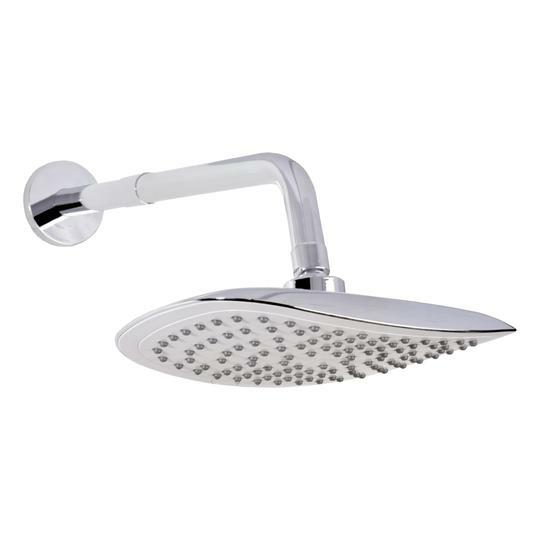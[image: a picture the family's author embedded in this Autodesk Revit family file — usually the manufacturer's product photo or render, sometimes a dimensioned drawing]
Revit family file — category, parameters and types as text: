
# Revit family: 01-1435-11 MEZCLADOR DUCHA 8” SIN SALIDA TOSCANA
name_source: partatom
category: Plumbing Fixtures
revit_build: Autodesk Revit 2018 (Build: 20170223_1515(x64)
units: mm (PartAtom-declared; Revit-internal decimal feet)

## family parameters
Cut with Voids When Loaded = No
Host = Face
OmniClass Number = 23.31.11.00
Part Type = Normal
Room Calculation Point = No
Round Connector Dimension = Use Diameter
Shared = No

## types (1)
- 01-1435-11
    Altura manija = 85 mm  [stored 0.278871 ft]
    Ancho escudo = 60 mm  [stored 0.19685 ft]
    CW Connection = Yes
    Default Elevation = 0 mm  [stored 0 ft]
    Description = Mezclador ducha
    Distancia entre griferias = 203.2 mm  [stored 0.666667 ft]
    HW Connection = Yes
    Link Ficha Tecnica = https://infotecnica.gricol.com
    Manija = 70 mm
    Manufacturer = Gricol
    Metal Zamak Cromado = Metal Zamak Cromado
    Model = 01-1435-11
    Plastico ABS Cromado = Plastico - ABS Cromado
    Product Name = MEZCLADOR DUCHA 8” SIN SALIDA TOSCANA
    Type Image = <None>
    URL = https://www.gricol.com
    Vent Connection = No
    Waste Connection = No

note: [stored X ft] marks values corroborated as IEEE doubles in the binary element streams (Revit-internal decimal feet)

## geometry (parser evidence)
native form markers: Blend x2, Sweep x16
no freeform markers — native parametric forms only
